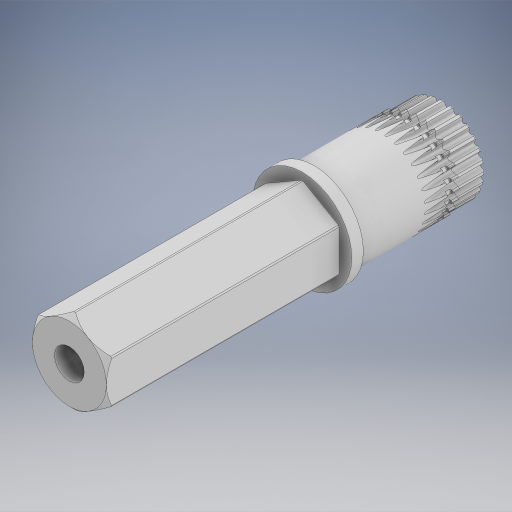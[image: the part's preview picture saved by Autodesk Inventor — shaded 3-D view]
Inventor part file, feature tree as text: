
AUTODESK INVENTOR PART (.ipt)
format: ipt  version: 2024.2 (Build 282272000, 272)  size: 1,484,288 bytes
history: native  units: in
note: dims shown in document units (in); Inventor stores cm internally (conversion verified against a paired STEP export)
features: fillet x1
ambient origin geometry x8: Origin, YZ Plane, XZ Plane, XY Plane, X Axis, Y Axis, Z Axis, Center Point
bodies: Solid1 (feature_tree)
feature tree (1):
  fillet  "Fillet5"  [1 undecoded]
note: 1 required parameter value undecoded (feature->parameter linkage not recoverable at this tier; creation-order binding heuristic only, values carry confidence <= 0.55)
